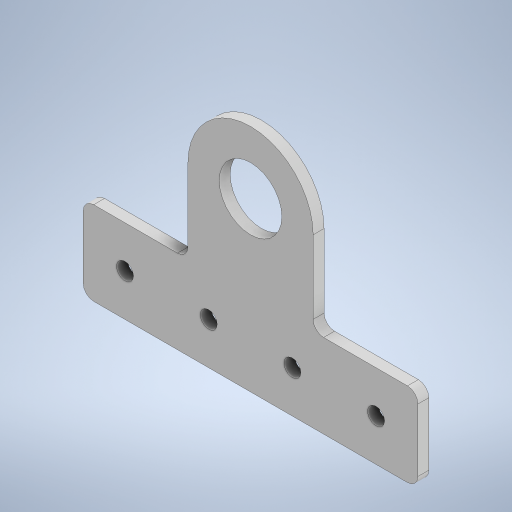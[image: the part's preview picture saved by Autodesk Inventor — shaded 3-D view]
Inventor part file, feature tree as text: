
AUTODESK INVENTOR PART (.ipt)
format: ipt  version: 2024 (Build 280153000, 153)  size: 273,920 bytes
history: native  units: in
note: dims shown in document units (in); Inventor stores cm internally (conversion verified against a paired STEP export)
features: extrude x1, fillet x1, sketch x1
ambient origin geometry x8: Origin, YZ Plane, XZ Plane, XY Plane, X Axis, Y Axis, Z Axis, Center Point
bodies: Solid1 (feature_tree)
feature tree (3):
  extrude  "Extrusion1"  Depth=0.748in
  fillet  "Fillet1"  Radius=0.13in
  sketch  "Sketch1"  dims[d0=1.4961in d1=0.748in d8=0.13in d9=0.0in d10=0.203in d11=0.203in d12=0.5in d13=0.5in d14=0.5in d15=0.5in d16=2.0in d17=1.0in d18=4.0in d19=2.0in d20=1.0in d21=1.0in d22=0.125in]
